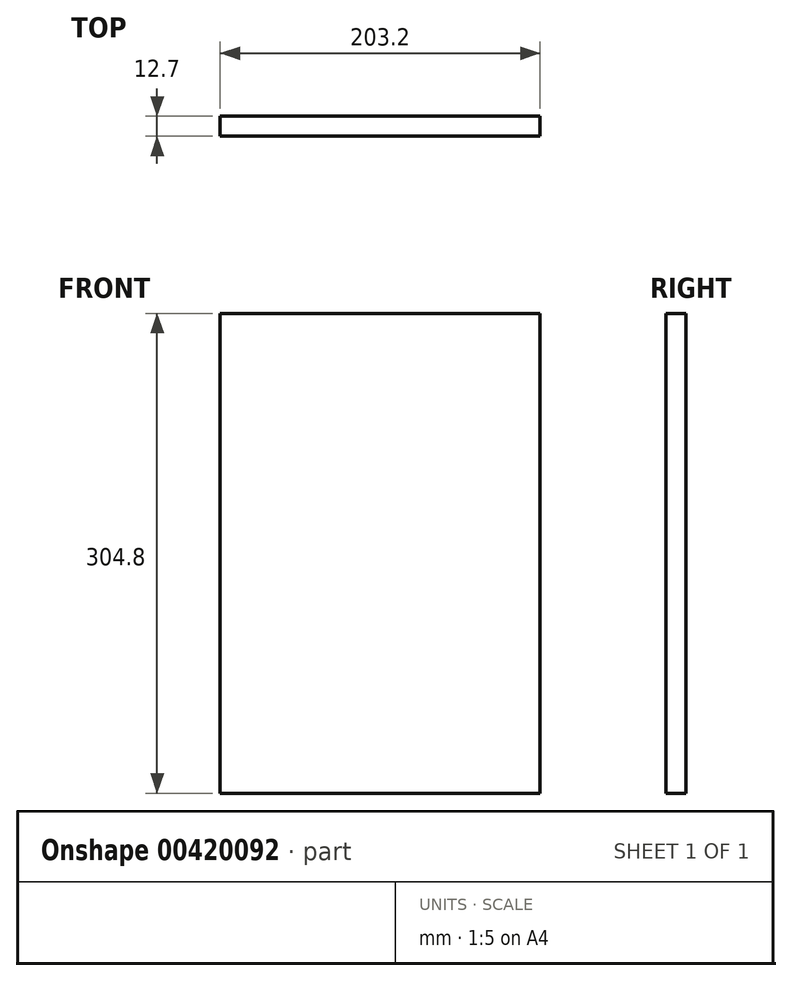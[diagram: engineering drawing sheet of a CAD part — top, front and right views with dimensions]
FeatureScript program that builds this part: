
annotation { "Feature Type Name" : "Feature", "Feature Type Description" : "" }
export const myFeature = defineFeature(function(context is Context, id is Id, definition is map)
    precondition{}
    {
        {
            var Q0;
            Q0=qCreatedBy(makeId("Front.planeOp"),FACE);
            var sketch = newSketch(context, id + "F0", { "sketchPlane" : qUnion([Q0])});
            skLineSegment(sketch, "E0.bottom", {"start": v(-107.05, 246.5) * mm, "end": v(96.15, 246.5) * mm});
            skLineSegment(sketch, "E0.top", {"start": v(-107.05, -58.3) * mm, "end": v(96.15, -58.3) * mm});
            skLineSegment(sketch, "E0.left", {"start": v(-107.05, 246.5) * mm, "end": v(-107.05, -58.3) * mm});
            skLineSegment(sketch, "E0.right", {"start": v(96.15, 246.5) * mm, "end": v(96.15, -58.3) * mm});
            skSolve(sketch);
        }
        {
            var Q0;
            Q0 = qSketchRegion(id + "F0", true);
            extrude(context, id + "F1", {"entities" : qUnion([Q0]), "depth" : 12.7 * mm});
        }
    });
